# Revit family: QF_ELECTROLUXPROFESSIONAL_1LSN2X_TD6-6_E
name_source: partatom
category: Attrezzature speciali
units: mm (PartAtom-declared; Revit-internal decimal feet)

## family parameters
Basato su piano di lavoro = No
Condiviso = No
Punto di calcolo locali = No
Quota connettore circolare = Usa diametro
Sempre verticale = Sì
Taglio con vuoti quando caricato = No
Tipo di parte = Normale

## types (31) — shared parameters
Depth Actual = 597 mm
Height Actual = 839 mm  [stored 2.75262 ft]
Latent Heat Output = 0.0
Length Actual = 715 mm  [stored 2.3458 ft]
Modello = TD6-6
Produttore = Electrolux Professional
Sensible Heat Output = 0.0
URL = www.electroluxprofessional.com
Weight = 58
zero-valued in all types: Gas KW, Prospetto di default, Steam Pounds per Hour

## per-type parameters (varying)
| type | Cycle | Descrizione | Item Number | Phase | Volts | Watts |
| 9872130086 | 60 Hz | TUMBLE DRYER TD6-6 6KG/13LB SST DRUM EL 5,1KW 200/60/3 COMPASS PRO 6G85 SLVR/SLVR DO.LEFT ELS-NETW. REV MB XT.CON | 1LT6HE | 3 | 200 V | 5400 W |
| 9872130036 | 60 Hz | TUMBLE DRYER TD6-6 MARINE 6KG/13LB SST DRUM EL 3,2KW 230/60/1N COMPASS PRO 6G81 SLVR/SLVR DO.LEFT REV MB XT.CON | 1L0ERZ | 1 | 230 V | 3500 W |
| 9872130006 | 50 Hz | TUMBLE DRYER TD6-6 CONDENSE 6KG/13LB SST DRUM EL 3KW 230/50/1 COMPASS PRO 6G81 SLVR/SLVR DO.LEFT REV MB XT.CON | 1LSN3H | 1 | 230 V | 3300 W |
| 9872130083 | 50 Hz | TUMBLE DRYER TD6-6 6KG/13LB SST DRUM EL 3,2KW 230/50/1N COMPASS PRO 6L80 2.I/O SLVR/SLVR DO.LEFT EXT.PM. REV XT.CON | 1LT6F1 | 1 | 230 V | 3500 W |
| 9872130046 | 50 Hz | TUMBLE DRYER TD6-6 6KG/13LB SST DRUM EL 5,1KW 400/50/3N COMPASS PRO 6L80 2.I/O SLVR/SLVR DO.LEFT EXT.PM. REV XT.CON | 1L0FTX | 3 | 400 V | 5400 W |
| 9872130056 | 50 Hz | TUMBLE DRYER TD6-6 CONDENSE 6KG/13LB SST DRUM EL 3KW 400/50/3N COMPASS PRO 6G81 SLVR/SLVR DO.LEFT REV MB XT.CON | 1L0GAR | 3 | 400 V | 3300 W |
| 9872130003 | 60 Hz | TUMBLE DRYER TD6-6 MARINE CONDENSE 6KG/13LB SST DRUM EL 3KW 440/60/3 COMPASS PRO 6G81 SLVR/SLVR DO.LEFT REV MB XT.CON | 1LSN3E | 3 | 440 V | 3300 W |
| 9872130080 | 50 Hz | TUMBLE DRYER TD6-6 MARINE CONDENSE 6KG/13LB SST DRUM EL 3KW 400/50/3 COMPASS PRO 6G81 SLVR/SLVR DO.LEFT REV MB XT.CON | 1LT6EB | 3 | 400 V | 3300 W |
| 9872130090 | 60 Hz | TUMBLE DRYER TD6-6 CONDENSE 6KG/13LB SST DRUM EL 3KW 400/60/3N COMPASS PRO 6G81 SLVR/SLVR DO.LEFT REV MB XT.CON | 1LT6KC | 3 | 400 V | 3300 W |
| 9872130040 | 50 Hz | TUMBLE DRYER TD6-6 6KG/13LB SST DRUM EL 3,2KW 230/50/1N COMPASS PRO 6G81 SLVR/SLVR DO.LEFT REV MB XT.CON | 1L0ES3 | 1 | 230 V | 3500 W |
| 9872130038 | 50 Hz | TUMBLE DRYER TD6-6 6KG/13LB SST DRUM EL 5,1KW 230/50/3 COMPASS PRO 6G81 SLVR/SLVR DO.LEFT REV MB XT.CON | 1L0ES1 | 3 | 230 V | 5400 W |
| 9872130085 | 50 Hz | TUMBLE DRYER TD6-6 6KG/13LB SST DRUM EL 5,1KW 200/50/3 COMPASS PRO 6G85 SLVR/SLVR DO.LEFT ELS-NETW. REV MB XT.CON | 1LT6HD | 3 | 200 V | 5400 W |
| 9872130078 | 60 Hz | TUMBLE DRYER TD6-6 CONDENSE 6KG/13LB SST DRUM EL 3KW 200/60/3 COMPASS PRO 6G85 SLVR/SLVR DO.LEFT REV MB XT.CON | 1LT6CE | 3 | 200 V | 3300 W |
| 9872130058 | 50 Hz | TUMBLE DRYER TD6-6 6KG/13LB SST DRUM EL 5,1KW 400/50/3N COMPASS PRO 6G81 SLVR/SLVR DO.LEFT REV MB XT.CON | 1LSPDJ | 3 | 400 V | 5400 W |
| 9872130005 | 50 Hz | TUMBLE DRYER TD6-6 CONDENSE 6KG/13LB SST DRUM EL 3KW 400/50/3N COMPASS PRO 6L80 2.I/O SLVR/SLVR DO.LEFT EXT.PM. REV ... | 1LSN3G | 3 | 400 V | 3300 W |
| 9872130015 | 50 Hz | TUMBLE DRYER TD6-6 6KG/13LB SST DRUM EL 5,1KW 400/50/3N COMPASS PRO 6A81 SLVR/SLVR DO.LEFT REV MB XT.CON | 1LSN3T | 3 | 400 V | 5400 W |
| 9872130082 | 50 Hz | TUMBLE DRYER TD6-6 6KG/13LB SST DRUM EL 3,2KW 230/50/1N COMPASS PRO 6G81 SST/SLVR DO.LEFT REV MB XT.CON | 1LT6EE | 1 | 230 V | 3500 W |
| 9872130092 | 60 Hz | TUMBLE DRYER TD6-6 MARINE 6KG SST DRUM EL 5,1KW 230/60/3 COMPASS PRO 6A81 SLVR/SLVR DO.LEFT REV MB XT.CON | 1LT6SX | 3 | 230 V | 5400 W |
| 9872130002 | 50 Hz | TUMBLE DRYER TD6-6 CONDENSE 6KG/13LB SST DRUM EL 3KW 400/50/3N COMPASS PRO 6G81 SLVR/SLVR DO.LEFT REV MB XT.CON | 1LSN3D | 3 | 400 V | 3300 W |
| 9872130057 | 50 Hz | TUMBLE DRYER TD6-6 6KG/13LB SST DRUM EL 3,2KW 230/50/1N COMPASS PRO 6G81 SLVR/SLVR DO.LEFT REV MB XT.CON | 1LSPDH | 1 | 230 V | 3500 W |
| 9872130084 | 50 Hz | TUMBLE DRYER TD6-6 6KG/13LB SST DRUM EL 3,2KW 230/50/1N COMPASS PRO 6L80 2.I/O SLVR/SLVR DO.LEFT EXT.PM. REV XT.CON | 1LT6F9 | 1 | 230 V | 3500 W |
| 9872130004 | 50 Hz | TUMBLE DRYER TD6-6 MARINE CONDENSE 6KG/13LB SST DRUM EL 3KW 400/50/3 COMPASS PRO 6G81 SLVR/SLVR DO.LEFT REV MB XT.CON | 1LSN3F | 3 | 400 V | 3300 W |
| 9872130014 | 50 Hz | TUMBLE DRYER TD6-6 6KG/13LB SST DRUM EL 5,1KW 400/50/3N COMPASS PRO 6G81 SLVR/SLVR DO.LEFT REV MB XT.CON | 1LSN3S | 3 | 400 V | 5400 W |
| 9872130081 | 60 Hz | TUMBLE DRYER TD6-6 MARINE CONDENSE 6KG/13LB SST DRUM EL 3KW 230/60/3 COMPASS PRO 6G81 /-ERROR- VALUE-ID FOR PNC=9872... | 1LT6EC | 3 | 230 V | 3300 W |
| 9872130044 | 60 Hz | TUMBLE DRYER TD6-6 MARINE 6KG/13LB SST DRUM EL 3,2KW 230/60/1 COMPASS PRO 6G81 SLVR/SLVR DO.LEFT REV MB XT.CON | 1L0FXS | 1 | 230 V | 3500 W |
| 9872130001 | 50 Hz | TUMBLE DRYER TD6-6 CONDENSE 6KG/13LB SST DRUM EL 3KW 400/50/3N COMPASS PRO 6A81 SLVR/SLVR DO.LEFT REV MB XT.CON | 1LSN3C | 3 | 400 V | 3300 W |
| 9872130041 | 60 Hz | TUMBLE DRYER TD6-6 MARINE 6KG/13LB SST DRUM EL 5,1KW 440/60/3 COMPASS PRO 6G81 SLVR/SLVR DO.LEFT REV MB XT.CON | 1L0ES4 | 3 | 440 V | 5400 W |
| 9872130089 | 60 Hz | TUMBLE DRYER TD6-6 MARINE CONDENSE 6KG/13LB SST DRUM EL 3KW 440/60/3 COMPASS PRO 6G81 SST/SLVR DO.LEFT REV MB XT.CON | 1LT6KA | 3 | 440 V | 3300 W |
| 9872130039 | 50 Hz | TUMBLE DRYER TD6-6 MARINE 6KG/13LB SST DRUM EL 5,1KW 400/50/3 COMPASS PRO 6G81 SLVR/SLVR DO.LEFT REV MB XT.CON | 1L0ES2 | 3 | 400 V | 5400 W |
| 9872130069 | 50 Hz | TUMBLE DRYER TD6-6 MARINE 6KG/13LB SST DRUM EL 5,1KW 400/50/3 COMPASS PRO 6G81 SLVR/SLVR DO.LEFT REV MB XT.CON | 1L0H2K | 3 | 400 V | 5400 W |
| 9872130079 | 50 Hz | TUMBLE DRYER TD6-6 CONDENSE 6KG/13LB SST DRUM EL 3KW 200/50/3 COMPASS PRO 6G85 SLVR/SLVR DO.LEFT REV MB XT.CON | 1LT6CF | 3 | 200 V | 3300 W |

note: [stored X ft] marks values corroborated as IEEE doubles in the binary element streams (Revit-internal decimal feet)

## geometry (parser evidence)
native form markers: Blend x6
no freeform markers — native parametric forms only
